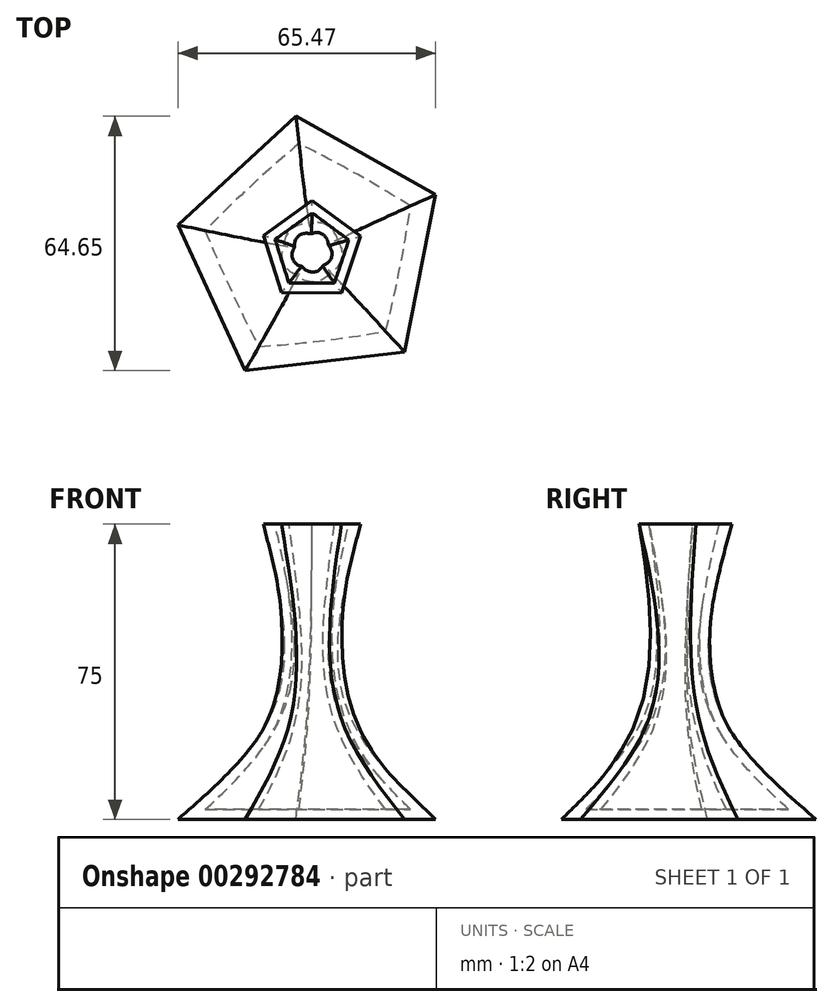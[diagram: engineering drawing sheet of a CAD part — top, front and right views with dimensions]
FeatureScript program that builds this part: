
annotation { "Feature Type Name" : "Feature", "Feature Type Description" : "" }
export const myFeature = defineFeature(function(context is Context, id is Id, definition is map)
    precondition{}
    {
        {
            var Q0;
            Q0=qCreatedBy(makeId("Top.planeOp"),FACE);
            cPlane(context, id + "F0", {"entities" : qUnion([Q0]), "cplaneType" : CPlaneType.OFFSET, "offset" : 25 * mm, "width" : 150 * mm, "height" : 150 * mm});
        }
        {
            var Q0;
            Q0=qCreatedBy(id+"F0.planeOp",FACE);
            cPlane(context, id + "F1", {"entities" : qUnion([Q0]), "cplaneType" : CPlaneType.OFFSET, "offset" : 50 * mm, "width" : 150 * mm, "height" : 150 * mm});
        }
        {
            var Q0;
            Q0=qCreatedBy(makeId("Top.planeOp"),FACE);
            var sketch = newSketch(context, id + "F2", { "sketchPlane" : qUnion([Q0])});
            skCircle(sketch, "E0.cCircle", {"center": v(0, 0) * mm, "radius": 28.04 * mm, "construction": true});
            skLineSegment(sketch, "E0.0", {"start": v(-4.06, 34.42) * mm, "end": v(31.48, 14.5) * mm});
            skLineSegment(sketch, "E0.1", {"start": v(31.48, 14.5) * mm, "end": v(23.52, -25.46) * mm});
            skLineSegment(sketch, "E0.2", {"start": v(23.52, -25.46) * mm, "end": v(-16.94, -30.23) * mm});
            skLineSegment(sketch, "E0.3", {"start": v(-16.94, -30.23) * mm, "end": v(-33.99, 6.77) * mm});
            skLineSegment(sketch, "E0.4", {"start": v(-33.99, 6.77) * mm, "end": v(-4.06, 34.42) * mm});
            skPoint(sketch, "E0.0.midPoint", {"position": v(13.7, 24.46) * mm});
            skSolve(sketch);
        }
        {
            var Q0;
            Q0=qCreatedBy(id+"F0.planeOp",FACE);
            var sketch = newSketch(context, id + "F3", { "sketchPlane" : qUnion([Q0])});
            skCircle(sketch, "E1", {"center": v(0, 0) * mm, "radius": 11.3 * mm});
            skSolve(sketch);
        }
        {
            var Q0;
            Q0=qCreatedBy(id+"F1.planeOp",FACE);
            var sketch = newSketch(context, id + "F4", { "sketchPlane" : qUnion([Q0])});
            skCircle(sketch, "E2.cCircle", {"center": v(0, 0) * mm, "radius": 10.5 * mm, "construction": true});
            skLineSegment(sketch, "E2.0", {"start": v(12.37, 3.92) * mm, "end": v(7.55, -10.56) * mm});
            skLineSegment(sketch, "E2.1", {"start": v(7.55, -10.56) * mm, "end": v(-7.7, -10.44) * mm});
            skLineSegment(sketch, "E2.2", {"start": v(-7.7, -10.44) * mm, "end": v(-12.31, 4.1) * mm});
            skLineSegment(sketch, "E2.3", {"start": v(-12.31, 4.1) * mm, "end": v(0.1, 12.98) * mm});
            skLineSegment(sketch, "E2.4", {"start": v(0.1, 12.98) * mm, "end": v(12.37, 3.92) * mm});
            skPoint(sketch, "E2.0.midPoint", {"position": v(9.96, -3.32) * mm});
            skSolve(sketch);
        }
        {
            var Q0;
            Q0=makeQuery(id+"F2.imprint","IMPRINT",FACE,{"disambiguationData":[TD([[makeQuery(id+"F2.imprint","IMPRINT",EDGE,{"derivedFrom":sQuery(id+"F2.wireOp",EDGE,"E0.0")}),-1.0]])]});
            var Q1;
            Q1=makeQuery(id+"F3.imprint","IMPRINT",FACE,{"disambiguationData":[TD([[makeQuery(id+"F3.imprint","IMPRINT",EDGE,{"derivedFrom":sQuery(id+"F3.wireOp",EDGE,"E1")}),1.0]])]});
            var Q2;
            Q2=makeQuery(id+"F4.imprint","IMPRINT",FACE,{"disambiguationData":[TD([[makeQuery(id+"F4.imprint","IMPRINT",EDGE,{"derivedFrom":sQuery(id+"F4.wireOp",EDGE,"E2.0")}),-1.0]])]});
            loft(context, id + "F5", {"sheetProfilesArray" : [{ "sheetProfileEntities" : qUnion([Q0]) }, { "sheetProfileEntities" : qUnion([Q1]) }, { "sheetProfileEntities" : qUnion([Q2]) }]});
        }
        {
            var Q0;
            Q0=makeQuery(id+"F5.opLoft","CAP_FACE",FACE,{"disambiguationData":[OSD([makeQuery(id+"F4.imprint","IMPRINT",FACE,{"disambiguationData":[TD([[makeQuery(id+"F4.imprint","IMPRINT",EDGE,{"derivedFrom":sQuery(id+"F4.wireOp",EDGE,"E2.0")}),-1.0]])]})])],"isStart":true});
            shell(context, id + "F6", {"entities" : qUnion([Q0]), "thickness" : 2.5 * mm});
        }
    });
